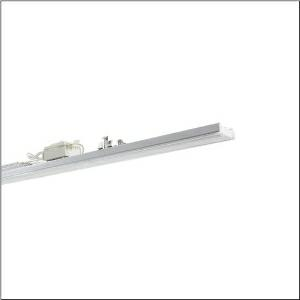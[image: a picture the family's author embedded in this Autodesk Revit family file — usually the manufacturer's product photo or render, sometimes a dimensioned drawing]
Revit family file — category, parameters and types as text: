
# Revit family: licross_11_recessed_mo_51tl12dn695g
name_source: partatom
category: Lighting Fixtures
units: mm (PartAtom-declared; Revit-internal decimal feet)

## family parameters
Cut with Voids When Loaded = No
Host = Face
Light Source = No
Part Type = Normal
Room Calculation Point = No
Round Connector Dimension = Use Diameter
Shared = No

## types (1)
- --- (1 x LED, 9990 lm, 56.7 W, 6500K)
    Apparent Load = 57 VA
    CIE Flux Codes = 67 92 99 100 100
    Color Rendering = 80
    Color Temperature = 6500K
    Default Elevation = 1800 mm
    Description = Licross 11 Recessed MO, luminaire insert, of sheet steel, coil coated, white, length: 1.500mm, width: 66mm, height: 67mm, LED rated luminous flux: 9.990lm, light colour: 865, SDCM (Standard Deviation of Colour Matching)MacAdam ≤ 2 SDCM (initial), control gear: DALI 2, with plug, 5-pole, with phase selection, mains connection: 220..240V, AC, 50/60Hz, rated input power: 57W, internal wiring halogen-free, primary optical cover: cover, of PMMA, light emission: direct distribution, primary light characteristic: symmetric, protection rating (complete): IP40, insulation class (complete): insulation class I (protective earthing), certification: CE, ENEC, VDE, UKCA, protection symbol: D if used in an environment without relevant dust loads with corresponding accessories, impact resistance: IK06, permissible ambient temperature for indoor applications: -25..+35°C, corresponds to IFS (International Featured Standards) requirements for safety and quality in the food industry, reducing of maximum allowable ambient temperature of 5°C with ceiling mounting, LABS conformity tested according to VDMA 24364:2018-05, The light source and the operating device comply with the requirements of the Ecodesign Regulation (EU) 2019/2020 and are replaceable in accordance with this regulation, packaging unit: 1 piece
    Height = 58 mm
    Lamp = 1 x LED
    Lamp Light Flux = 9990 lm
    Lamp Power = 56.7 W
    Lamp count = 1
    Length = 1500 mm
    Luminous efficacy = 176 lm/W
    Manufacturer = Siteco
    ModVariant = No
    Model = 51TL12DN695G
    Mounting Place = Ceiling
    Mounting Type = Pendant
    Number of Poles = 1
    OnlyDefault = Yes
    Power Factor = 1
    Product Name = Licross 11 Recessed MO
    Product group = luminaire insert | ceiling pendant
    ProductGroupID = 901
    Protection Class = Protection class I
    Protection Degree = IP 40
    RLX_Detail_Level = 1
    RLX_Emergency_Light_Flux = 0 lm
    RLX_Emergency_Type = 0
    RLX_Emergency_Type_DB = No
    RlxData = <blob elided: 24585 chars, md5=daa5b3b8>
    Socket = socket
    Standby Power = 0 W
    System Light Flux = 9990 lm
    System Power = 57 W
    Type Comments = factory setting: luminous flux: 100 % | dim-lin: 254 | 378 mA
    Type Image = l_1296930.jpg
    URL = http://relux.com
    VarID = @adj_075539
    Voltage = 0 V
    Weight = 0.00 kg
    Width = 66 mm

## geometry (parser evidence)
native form markers: Blend x4, Sweep x11
no freeform markers — native parametric forms only
